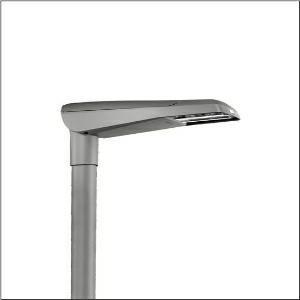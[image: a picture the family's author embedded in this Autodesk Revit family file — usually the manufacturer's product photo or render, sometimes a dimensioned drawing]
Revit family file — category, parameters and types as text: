
# Revit family: streetlight_sl_11_iq_micro___st1_2a_5xc1a51f08ce_9ca9
name_source: partatom
category: Lighting Fixtures
units: mm (PartAtom-declared; Revit-internal decimal feet)

## family parameters
Cut with Voids When Loaded = No
Host = Face
Light Source = No
Part Type = Normal
Room Calculation Point = No
Round Connector Dimension = Use Diameter
Shared = No

## types (1)
- --- (1 x LED, 1880 lm, 12.6 W, 3000K)
    Apparent Load = 13 VA
    CIE Flux Codes = 33 71 96 100 100
    Color Rendering = 70
    Color Temperature = 3000K
    Default Elevation = 1800 mm
    Description = Streetlight SL 11 iQ micro, mast luminaire, primary light control with 3 zone facetted reflector, of plastic, silver coated, highly specular, primary optical cover: cover, of PMMA, transparent, light distribution: ST1.2a, light emission: direct distribution, primary light characteristic: asymmetric, installation type: post-top, side-entry, lamps: LED, High Power LED, rated values: 1.880lm | 12,6W | 149,2lm/W (begin service life); end service life: 1.880lm | 12,9W; at 50% lumin. flux: 940lm | 6,8W | 138,2lm/W, colour temperature: 3000K, colour rendering: CRI > 70, light colour: 730, light setting 1 begin service life: 100% | 1.880lm | 12,6W | 149,2lm/W | 3.000K, light setting 1 end service life: 12,9W, further light settings possible, control: Street-Remote, optimised constant luminous flux control (CLO 2.0), Desk-Remote (wireless, voltage-free reading and setting of iQ features in the workshop via application-optimized NFC function/RFID function), Light-Fading, Smart-Wire, Night-Set, Lumen-Switch, Temp-Guard, Auto-Match, with cable H07RN-F 5x 1.5mm², mains connection: 230..240V, AC, 50/60Hz, connection cable pre-assembled, cable length: 5,5m, luminaire housing, of diecast aluminium, powder-coated, Siteco® metallic grey (DB 702S), please order mast flange separately, inclination adjustable without tools: 0°, 5°, 10°, 15° (post-top) | 0°, -5°, -10°, -15° (side-entry), sealing non-destructively replaceable, multi-level sealing system, length: 600mm, width: 174mm, height: 116mm, mast flange for spigot size: 42mm (side-entry): 5XC10008XM4, 60/48mm (side-entry/post-top): 5XC10108XM2, 76/60mm (side-entry/post-top): 5XC10108XM1, equipment: standard, protection rating (complete): IP66, insulation class (complete): insulation class II (safety insulation), certification: CE, ENEC, ENEC+, VDE, impact resistance: IK10, permissible operating ambient temperature for outdoor applications: -25..+50°C, standard-compliant lighting for roads and squares, Environmental Product Declaration (EPD) tested and certified by an independent institute, packaging unit: 1 piece

Light Distribution: ST1.2a
    Height = 116 mm
    Lamp = 1 x LED
    Lamp Light Flux = 1880 lm
    Lamp Power = 12.6 W
    Lamp count = 1
    Length = 600 mm
    Luminous efficacy = 149 lm/W
    Manufacturer = Siteco
    ModVariant = No
    Model = 5XC1A51F08CE
    Number of Poles = 1
    OnlyDefault = Yes
    Power Factor = 1
    Product Name = Streetlight SL 11 iQ micro | ST1.2a
    Product group = mast luminaire | pylon top
    ProductGroupID = 6100
    Protection Class = Protection class II
    Protection Degree = IP 66
    RLX_Detail_Level = 1
    RLX_Emergency_Light_Flux = 0 lm
    RLX_Emergency_Type = 0
    RLX_Emergency_Type_DB = No
    RlxData = <blob elided: 26529 chars, md5=46986a7c>
    Socket = socket
    Standby Power = 0 W
    System Light Flux = 1880 lm
    System Power = 13 W
    Type Comments = factory setting: luminous flux: 100 % | dim-lin: 254 | 229 mA
    Type Image = l_1006566.jpg
    URL = http://relux.com
    VarID = @adj_018013
    Voltage = 0 V
    Weight = 0.00 kg
    Width = 174 mm

## geometry (parser evidence)
native form markers: Blend x4, Sweep x10
no freeform markers — native parametric forms only
